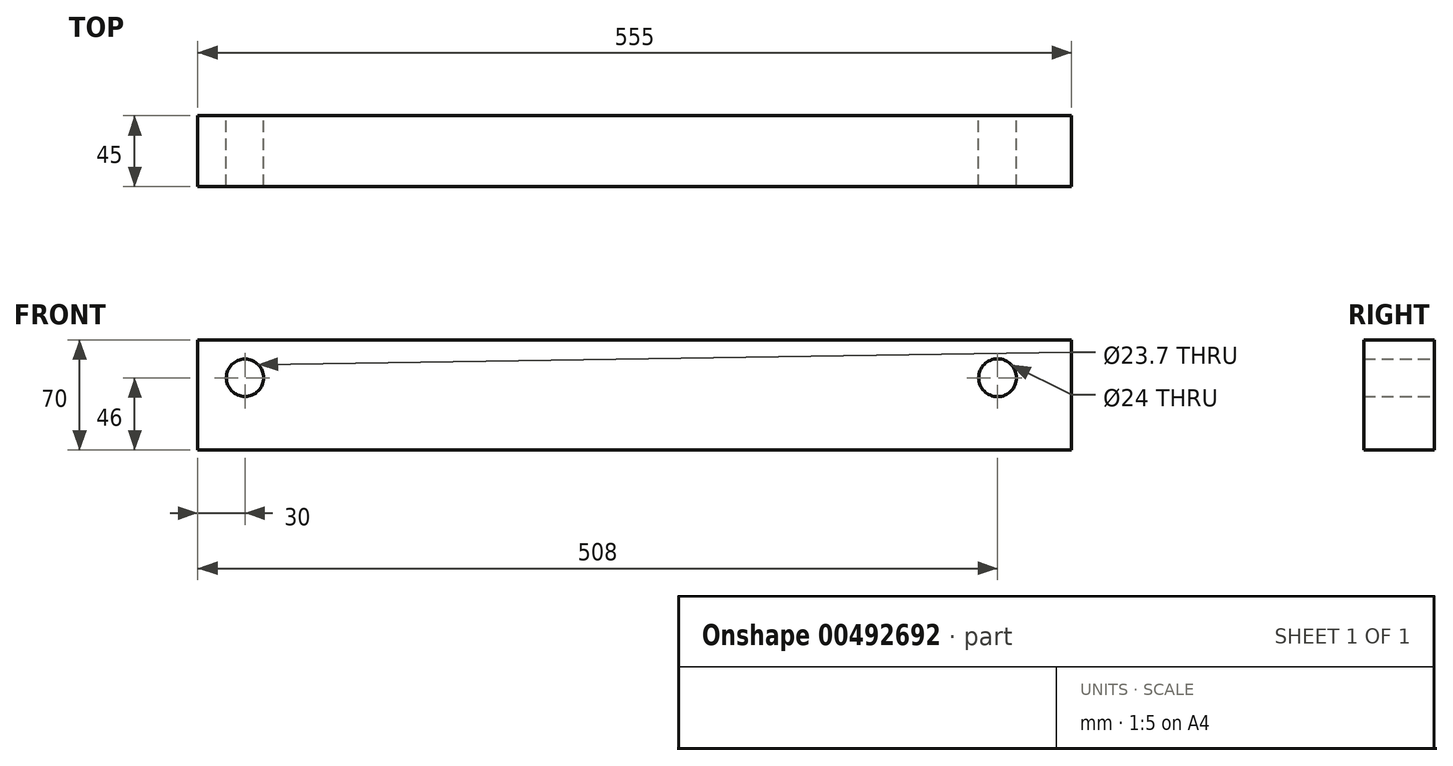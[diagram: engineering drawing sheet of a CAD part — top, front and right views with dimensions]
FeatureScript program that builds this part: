
annotation { "Feature Type Name" : "Feature", "Feature Type Description" : "" }
export const myFeature = defineFeature(function(context is Context, id is Id, definition is map)
    precondition{}
    {
        {
            var Q0;
            Q0=qCreatedBy(makeId("Front.planeOp"),FACE);
            var sketch = newSketch(context, id + "F0", { "sketchPlane" : qUnion([Q0])});
            skLineSegment(sketch, "E0.bottom", {"start": v(0, 0) * mm, "end": v(-555, 0) * mm});
            skLineSegment(sketch, "E0.top", {"start": v(0, -70) * mm, "end": v(-555, -70) * mm});
            skLineSegment(sketch, "E0.left", {"start": v(0, 0) * mm, "end": v(0, -70) * mm});
            skLineSegment(sketch, "E0.right", {"start": v(-555, 0) * mm, "end": v(-555, -70) * mm});
            skSolve(sketch);
        }
        {
            var Q0;
            Q0 = qSketchRegion(id + "F0", true);
            extrude(context, id + "F1", {"entities" : qUnion([Q0]), "depth" : 45 * mm});
        }
        {
            var Q0;
            Q0=makeQuery(id+"F1.opExtrude","CAP_FACE",FACE,{"disambiguationData":[OSD([sQuery(id+"F0.wireOp",EDGE,"E0.bottom"),sQuery(id+"F0.wireOp",EDGE,"E0.top"),sQuery(id+"F0.wireOp",EDGE,"E0.left"),sQuery(id+"F0.wireOp",EDGE,"E0.right")])],"isStart":true});
            var sketch = newSketch(context, id + "F2", { "sketchPlane" : qUnion([Q0])});
            skCircle(sketch, "E1", {"center": v(525, -24) * mm, "radius": 11.85 * mm});
            skSolve(sketch);
        }
        {
            var Q0;
            Q0 = qSketchRegion(id + "F2", true);
            extrude(context, id + "F3", {"entities" : qUnion([Q0]), "operationType" : NewBodyOperationType.REMOVE, "endBound" : BoundingType.THROUGH_ALL, "oppositeDirection" : true, "depth" : 25 * mm});
        }
        {
            var Q0;
            Q0=makeQuery(id+"F1.opExtrude","CAP_FACE",FACE,{"disambiguationData":[OSD([sQuery(id+"F0.wireOp",EDGE,"E0.bottom"),sQuery(id+"F0.wireOp",EDGE,"E0.top"),sQuery(id+"F0.wireOp",EDGE,"E0.left"),sQuery(id+"F0.wireOp",EDGE,"E0.right")])],"isStart":true});
            var sketch = newSketch(context, id + "F4", { "sketchPlane" : qUnion([Q0])});
            skCircle(sketch, "E2", {"center": v(47, -24) * mm, "radius": 12 * mm});
            skSolve(sketch);
        }
        {
            var Q0;
            Q0 = qSketchRegion(id + "F4", true);
            extrude(context, id + "F5", {"entities" : qUnion([Q0]), "operationType" : NewBodyOperationType.REMOVE, "endBound" : BoundingType.THROUGH_ALL, "oppositeDirection" : true, "depth" : 25 * mm});
        }
    });
